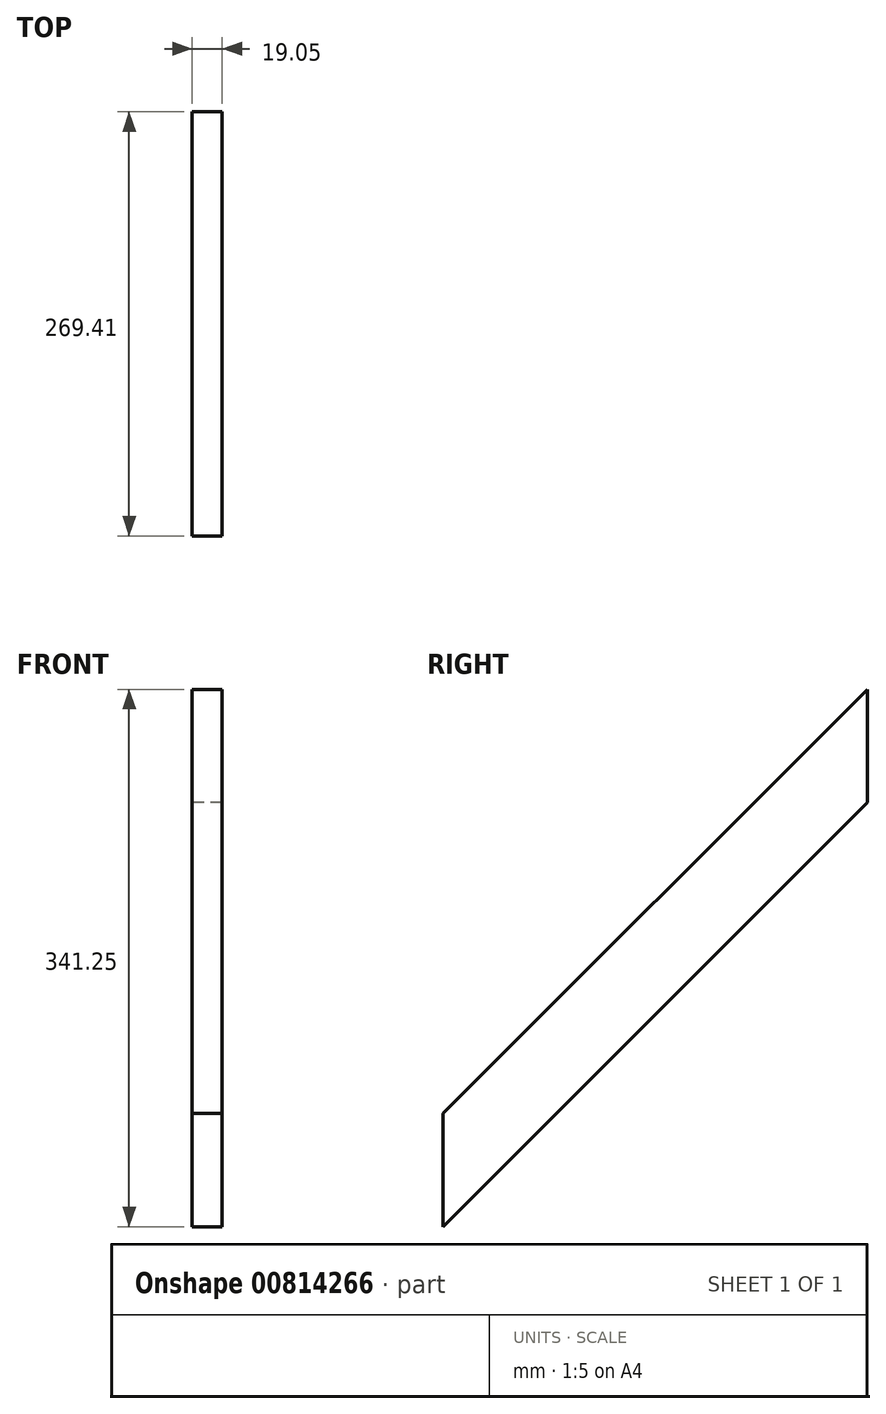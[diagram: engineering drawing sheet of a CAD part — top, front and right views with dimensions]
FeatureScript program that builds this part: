
annotation { "Feature Type Name" : "Feature", "Feature Type Description" : "" }
export const myFeature = defineFeature(function(context is Context, id is Id, definition is map)
    precondition{}
    {
        {
            var Q0;
            Q0=qCreatedBy(makeId("Right.planeOp"),FACE);
            var sketch = newSketch(context, id + "F0", { "sketchPlane" : qUnion([Q0])});
            skLineSegment(sketch, "E0", {"start": v(-269.4, 0) * mm, "end": v(0, 269.4) * mm});
            skLineSegment(sketch, "E1", {"start": v(-269.4, 0) * mm, "end": v(-269.4, -71.84) * mm});
            skLineSegment(sketch, "E2", {"start": v(-269.4, -71.84) * mm, "end": v(0, 197.57) * mm});
            skLineSegment(sketch, "E3", {"start": v(0, 197.57) * mm, "end": v(0, 269.4) * mm});
            skSolve(sketch);
        }
        {
            var Q0;
            Q0 = qSketchRegion(id + "F0", true);
            extrude(context, id + "F1", {"entities" : qUnion([Q0]), "depth" : 19.05 * mm, "offsetDistance" : 25.4 * mm});
        }
    });
